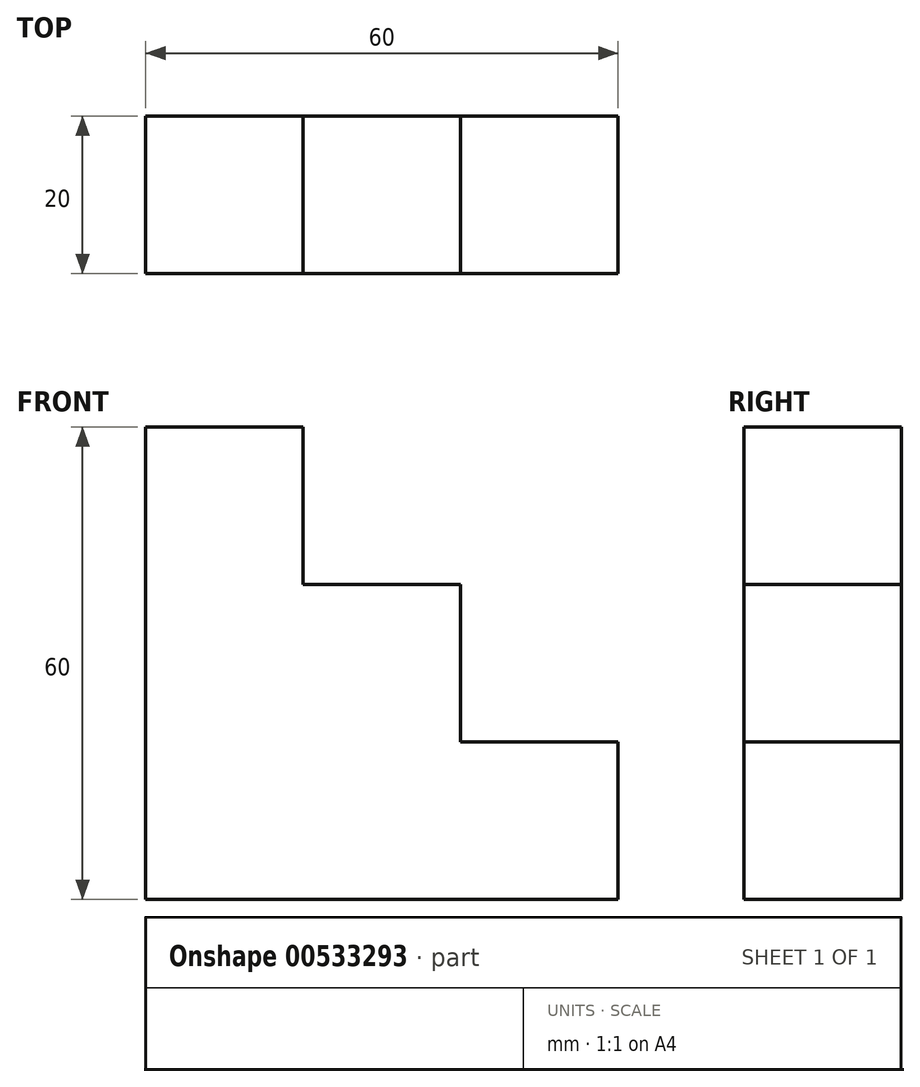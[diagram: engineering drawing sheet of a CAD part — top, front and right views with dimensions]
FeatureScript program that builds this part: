
annotation { "Feature Type Name" : "Feature", "Feature Type Description" : "" }
export const myFeature = defineFeature(function(context is Context, id is Id, definition is map)
    precondition{}
    {
        {
            var Q0;
            Q0=qCreatedBy(makeId("Front.planeOp"),FACE);
            var sketch = newSketch(context, id + "F0", { "sketchPlane" : qUnion([Q0])});
            skLineSegment(sketch, "E0", {"start": v(-78.98, 60) * mm, "end": v(-58.98, 60) * mm});
            skLineSegment(sketch, "E1", {"start": v(-58.98, 60) * mm, "end": v(-58.98, 40) * mm});
            skLineSegment(sketch, "E2", {"start": v(-58.98, 40) * mm, "end": v(-38.98, 40) * mm});
            skLineSegment(sketch, "E3", {"start": v(-38.98, 40) * mm, "end": v(-38.98, 20) * mm});
            skLineSegment(sketch, "E4", {"start": v(-38.98, 20) * mm, "end": v(-18.98, 20) * mm});
            skLineSegment(sketch, "E5", {"start": v(-18.98, 20) * mm, "end": v(-18.98, 0) * mm});
            skLineSegment(sketch, "E6", {"start": v(-18.98, 0) * mm, "end": v(-78.98, 0) * mm});
            skLineSegment(sketch, "E7", {"start": v(-78.98, 0) * mm, "end": v(-78.98, 60) * mm});
            skSolve(sketch);
        }
        {
            var Q0;
            Q0 = qSketchRegion(id + "F0", true);
            extrude(context, id + "F1", {"entities" : qUnion([Q0]), "depth" : 20 * mm, "offsetDistance" : 25 * mm});
        }
    });
